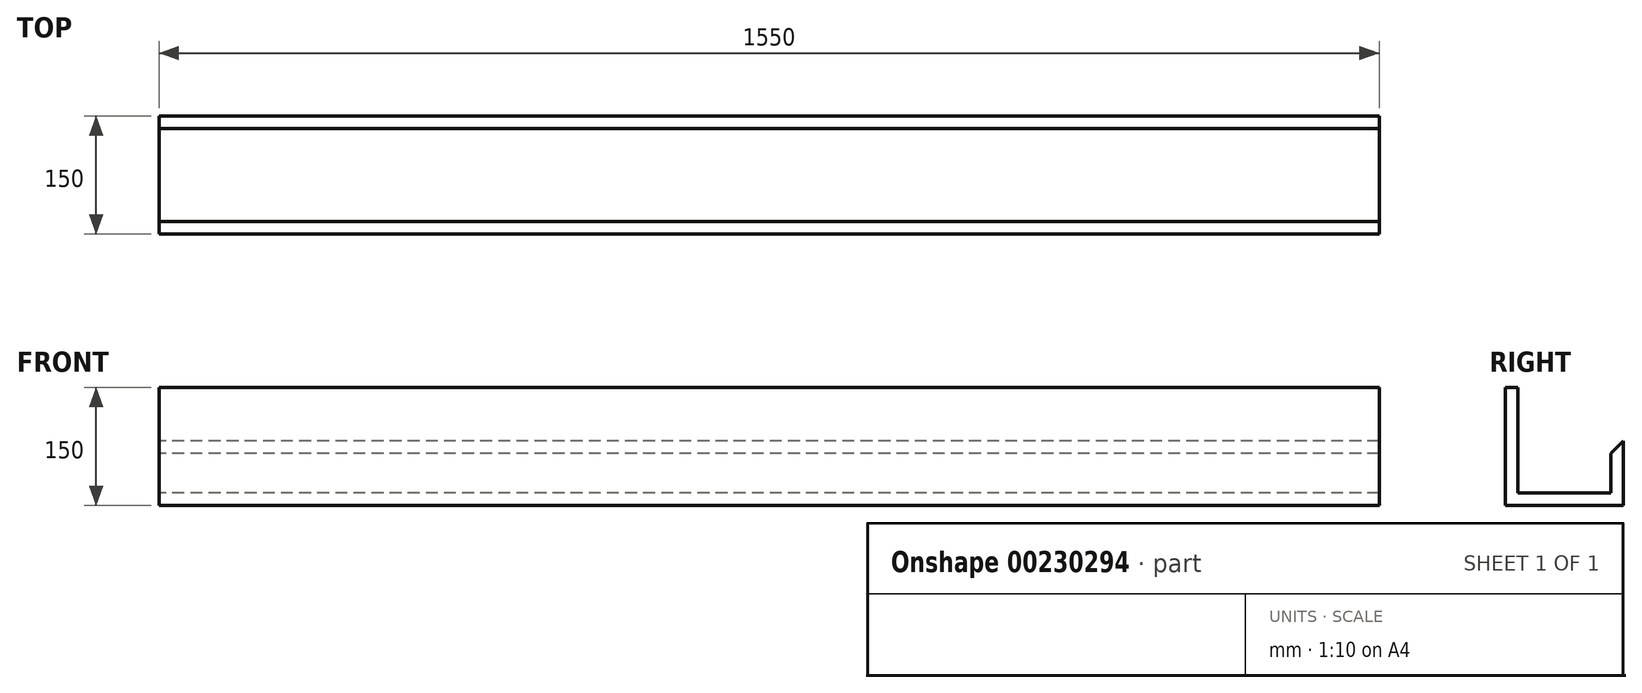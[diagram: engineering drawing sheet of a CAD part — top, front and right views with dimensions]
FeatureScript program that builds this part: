
annotation { "Feature Type Name" : "Feature", "Feature Type Description" : "" }
export const myFeature = defineFeature(function(context is Context, id is Id, definition is map)
    precondition{}
    {
        {
            var Q0;
            Q0=qCreatedBy(makeId("Right.planeOp"),FACE);
            var sketch = newSketch(context, id + "F0", { "sketchPlane" : qUnion([Q0])});
            skLineSegment(sketch, "E0", {"start": v(0, 0) * mm, "end": v(0, 150) * mm});
            skLineSegment(sketch, "E1", {"start": v(0, 150) * mm, "end": v(16, 150) * mm});
            skLineSegment(sketch, "E2", {"start": v(16, 150) * mm, "end": v(16, 16) * mm});
            skLineSegment(sketch, "E3", {"start": v(16, 16) * mm, "end": v(134, 16) * mm});
            skLineSegment(sketch, "E4", {"start": v(134, 16) * mm, "end": v(134, 66) * mm});
            skLineSegment(sketch, "E5", {"start": v(134, 66) * mm, "end": v(150, 82) * mm});
            skLineSegment(sketch, "E6", {"start": v(150, 82) * mm, "end": v(150, 0) * mm});
            skLineSegment(sketch, "E7", {"start": v(150, 0) * mm, "end": v(0, 0) * mm});
            skSolve(sketch);
        }
        {
            var Q0;
            Q0=makeQuery(id+"F0.imprint","IMPRINT",FACE,{"disambiguationData":[TD([[makeQuery(id+"F0.imprint","IMPRINT",EDGE,{"derivedFrom":sQuery(id+"F0.wireOp",EDGE,"E0")}),-1.0]])]});
            extrude(context, id + "F1", {"entities" : qUnion([Q0]), "depth" : 1550 * mm});
        }
    });
